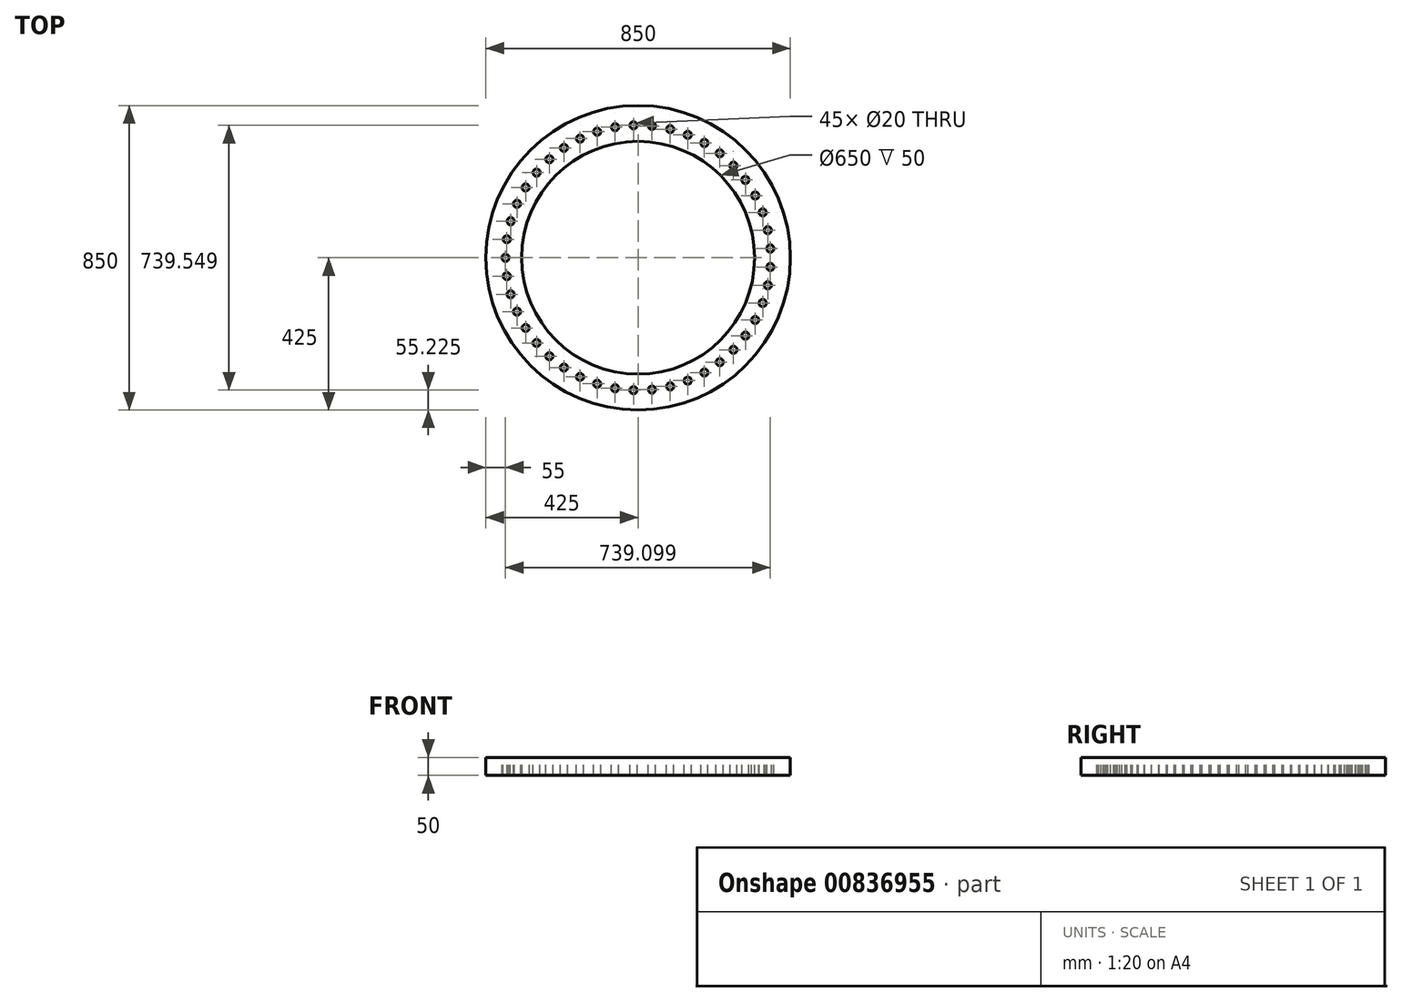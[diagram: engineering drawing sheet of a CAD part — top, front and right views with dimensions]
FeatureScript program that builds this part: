
annotation { "Feature Type Name" : "Feature", "Feature Type Description" : "" }
export const myFeature = defineFeature(function(context is Context, id is Id, definition is map)
    precondition{}
    {
        {
            var Q0;
            Q0=qCreatedBy(makeId("Top.planeOp"),FACE);
            var sketch = newSketch(context, id + "F0", { "sketchPlane" : qUnion([Q0])});
            skLineSegment(sketch, "E0.bottom", {"start": v(-1185, 450) * mm, "end": v(1185, 450) * mm});
            skLineSegment(sketch, "E0.top", {"start": v(-1185, -450) * mm, "end": v(1185, -450) * mm});
            skLineSegment(sketch, "E0.left", {"start": v(-1185, 450) * mm, "end": v(-1185, -450) * mm});
            skLineSegment(sketch, "E0.right", {"start": v(1185, 450) * mm, "end": v(1185, -450) * mm});
            skPoint(sketch, "E0.middle", {"position": v(0, 0) * mm});
            skLineSegment(sketch, "E1.bottom", {"start": v(-1185, 450) * mm, "end": v(-1141.5, 450) * mm});
            skLineSegment(sketch, "E1.top", {"start": v(-1185, -450) * mm, "end": v(-1141.5, -450) * mm});
            skLineSegment(sketch, "E1.right", {"start": v(-1141.49, 450) * mm, "end": v(-1141.49, -450) * mm});
            skLineSegment(sketch, "E2", {"start": v(1185, 0) * mm, "end": v(-1185, 0) * mm, "construction": true});
            skLineSegment(sketch, "E3", {"start": v(-92.5, -600) * mm, "end": v(-92.5, 600) * mm, "construction": true});
            skCircle(sketch, "E4", {"center": v(-92.5, 0) * mm, "radius": 600 * mm});
            skCircle(sketch, "E5", {"center": v(-92.5, 0) * mm, "radius": 550 * mm});
            skCircle(sketch, "E6", {"center": v(-92.5, 0) * mm, "radius": 425 * mm});
            skCircle(sketch, "E7", {"center": v(-92.5, 0) * mm, "radius": 525 * mm});
            skCircle(sketch, "E8", {"center": v(-617.5, 0) * mm, "radius": 10 * mm});
            skCircle(sketch, "E9.1.0", {"center": v(-612.4, -73.07) * mm, "radius": 10 * mm});
            skCircle(sketch, "E9.2.0", {"center": v(-597.16, -144.7) * mm, "radius": 10 * mm});
            skCircle(sketch, "E10.1.3.0", {"center": v(-572.11, -213.54) * mm, "radius": 10 * mm});
            skCircle(sketch, "E10.1.4.0", {"center": v(-537.73, -278.2) * mm, "radius": 10 * mm});
            skCircle(sketch, "E10.1.5.0", {"center": v(-494.67, -337.46) * mm, "radius": 10 * mm});
            skCircle(sketch, "E10.1.6.0", {"center": v(-443.8, -390.15) * mm, "radius": 10 * mm});
            skCircle(sketch, "E10.1.7.0", {"center": v(-386.08, -435.24) * mm, "radius": 10 * mm});
            skCircle(sketch, "E10.1.8.0", {"center": v(-322.64, -471.87) * mm, "radius": 10 * mm});
            skCircle(sketch, "E10.1.9.0", {"center": v(-254.73, -499.3) * mm, "radius": 10 * mm});
            skCircle(sketch, "E10.1.10.0", {"center": v(-183.67, -517.02) * mm, "radius": 10 * mm});
            skCircle(sketch, "E10.1.11.0", {"center": v(-110.82, -524.68) * mm, "radius": 10 * mm});
            skCircle(sketch, "E10.1.12.0", {"center": v(-37.62, -522.12) * mm, "radius": 10 * mm});
            skCircle(sketch, "E10.1.13.0", {"center": v(34.5, -509.4) * mm, "radius": 10 * mm});
            skCircle(sketch, "E10.1.14.0", {"center": v(104.17, -486.77) * mm, "radius": 10 * mm});
            skCircle(sketch, "E10.1.15.0", {"center": v(170, -454.66) * mm, "radius": 10 * mm});
            skCircle(sketch, "E10.1.16.0", {"center": v(230.72, -413.7) * mm, "radius": 10 * mm});
            skCircle(sketch, "E10.1.17.0", {"center": v(285.15, -364.7) * mm, "radius": 10 * mm});
            skCircle(sketch, "E10.1.18.0", {"center": v(332.23, -308.59) * mm, "radius": 10 * mm});
            skCircle(sketch, "E10.1.19.0", {"center": v(371.05, -246.47) * mm, "radius": 10 * mm});
            skCircle(sketch, "E10.1.20.0", {"center": v(400.84, -179.56) * mm, "radius": 10 * mm});
            skCircle(sketch, "E10.1.21.0", {"center": v(421.03, -109.15) * mm, "radius": 10 * mm});
            skCircle(sketch, "E10.1.22.0", {"center": v(431.22, -36.62) * mm, "radius": 10 * mm});
            skCircle(sketch, "E10.1.23.0", {"center": v(431.22, 36.62) * mm, "radius": 10 * mm});
            skCircle(sketch, "E10.1.24.0", {"center": v(421.03, 109.15) * mm, "radius": 10 * mm});
            skCircle(sketch, "E10.1.25.0", {"center": v(400.84, 179.56) * mm, "radius": 10 * mm});
            skCircle(sketch, "E10.1.26.0", {"center": v(371.05, 246.47) * mm, "radius": 10 * mm});
            skCircle(sketch, "E10.1.27.0", {"center": v(332.23, 308.59) * mm, "radius": 10 * mm});
            skCircle(sketch, "E10.1.28.0", {"center": v(285.15, 364.7) * mm, "radius": 10 * mm});
            skCircle(sketch, "E10.1.29.0", {"center": v(230.72, 413.7) * mm, "radius": 10 * mm});
            skCircle(sketch, "E10.1.30.0", {"center": v(170, 454.66) * mm, "radius": 10 * mm});
            skCircle(sketch, "E10.1.31.0", {"center": v(104.17, 486.77) * mm, "radius": 10 * mm});
            skCircle(sketch, "E10.1.32.0", {"center": v(34.5, 509.4) * mm, "radius": 10 * mm});
            skCircle(sketch, "E10.1.33.0", {"center": v(-37.62, 522.12) * mm, "radius": 10 * mm});
            skCircle(sketch, "E10.1.34.0", {"center": v(-110.82, 524.68) * mm, "radius": 10 * mm});
            skCircle(sketch, "E10.1.35.0", {"center": v(-183.67, 517.02) * mm, "radius": 10 * mm});
            skCircle(sketch, "E10.1.36.0", {"center": v(-254.73, 499.3) * mm, "radius": 10 * mm});
            skCircle(sketch, "E10.1.37.0", {"center": v(-322.64, 471.87) * mm, "radius": 10 * mm});
            skCircle(sketch, "E10.1.38.0", {"center": v(-386.08, 435.24) * mm, "radius": 10 * mm});
            skCircle(sketch, "E10.1.39.0", {"center": v(-443.8, 390.15) * mm, "radius": 10 * mm});
            skCircle(sketch, "E10.1.40.0", {"center": v(-494.67, 337.46) * mm, "radius": 10 * mm});
            skCircle(sketch, "E10.1.41.0", {"center": v(-537.73, 278.2) * mm, "radius": 10 * mm});
            skCircle(sketch, "E10.1.42.0", {"center": v(-572.11, 213.54) * mm, "radius": 10 * mm});
            skCircle(sketch, "E10.1.43.0", {"center": v(-597.16, 144.7) * mm, "radius": 10 * mm});
            skCircle(sketch, "E10.1.44.0", {"center": v(-612.4, 73.07) * mm, "radius": 10 * mm});
            skCircle(sketch, "E11", {"center": v(-92.5, 0) * mm, "radius": 370 * mm});
            skCircle(sketch, "E12", {"center": v(-462.5, 0) * mm, "radius": 10 * mm});
            skCircle(sketch, "E13.1.0", {"center": v(-458.9, -51.5) * mm, "radius": 10 * mm});
            skCircle(sketch, "E13.2.0", {"center": v(-448.17, -101.99) * mm, "radius": 10 * mm});
            skCircle(sketch, "E13.3.0", {"center": v(-430.51, -150.5) * mm, "radius": 10 * mm});
            skCircle(sketch, "E13.4.0", {"center": v(-406.28, -196.07) * mm, "radius": 10 * mm});
            skCircle(sketch, "E13.5.0", {"center": v(-375.94, -237.83) * mm, "radius": 10 * mm});
            skCircle(sketch, "E13.6.0", {"center": v(-340.08, -274.96) * mm, "radius": 10 * mm});
            skCircle(sketch, "E13.7.0", {"center": v(-299.4, -306.74) * mm, "radius": 10 * mm});
            skCircle(sketch, "E13.8.0", {"center": v(-254.7, -332.55) * mm, "radius": 10 * mm});
            skCircle(sketch, "E13.9.0", {"center": v(-206.84, -351.9) * mm, "radius": 10 * mm});
            skCircle(sketch, "E13.10.0", {"center": v(-156.75, -364.38) * mm, "radius": 10 * mm});
            skCircle(sketch, "E13.11.0", {"center": v(-105.41, -369.77) * mm, "radius": 10 * mm});
            skCircle(sketch, "E13.12.0", {"center": v(-53.82, -367.97) * mm, "radius": 10 * mm});
            skCircle(sketch, "E13.13.0", {"center": v(-2.99, -359) * mm, "radius": 10 * mm});
            skCircle(sketch, "E13.14.0", {"center": v(46.1, -343.06) * mm, "radius": 10 * mm});
            skCircle(sketch, "E13.15.0", {"center": v(92.5, -320.43) * mm, "radius": 10 * mm});
            skCircle(sketch, "E13.16.0", {"center": v(135.3, -291.56) * mm, "radius": 10 * mm});
            skCircle(sketch, "E13.17.0", {"center": v(173.66, -257.02) * mm, "radius": 10 * mm});
            skCircle(sketch, "E13.18.0", {"center": v(206.84, -217.48) * mm, "radius": 10 * mm});
            skCircle(sketch, "E13.19.0", {"center": v(234.2, -173.7) * mm, "radius": 10 * mm});
            skCircle(sketch, "E13.20.0", {"center": v(255.19, -126.55) * mm, "radius": 10 * mm});
            skCircle(sketch, "E13.21.0", {"center": v(269.41, -76.93) * mm, "radius": 10 * mm});
            skCircle(sketch, "E13.22.0", {"center": v(276.6, -25.8) * mm, "radius": 10 * mm});
            skCircle(sketch, "E13.23.0", {"center": v(276.6, 25.8) * mm, "radius": 10 * mm});
            skCircle(sketch, "E13.24.0", {"center": v(269.41, 76.93) * mm, "radius": 10 * mm});
            skCircle(sketch, "E13.25.0", {"center": v(255.19, 126.55) * mm, "radius": 10 * mm});
            skCircle(sketch, "E13.26.0", {"center": v(234.2, 173.7) * mm, "radius": 10 * mm});
            skCircle(sketch, "E13.27.0", {"center": v(206.84, 217.48) * mm, "radius": 10 * mm});
            skCircle(sketch, "E13.28.0", {"center": v(173.66, 257.02) * mm, "radius": 10 * mm});
            skCircle(sketch, "E13.29.0", {"center": v(135.3, 291.56) * mm, "radius": 10 * mm});
            skCircle(sketch, "E13.30.0", {"center": v(92.5, 320.43) * mm, "radius": 10 * mm});
            skCircle(sketch, "E13.31.0", {"center": v(46.1, 343.06) * mm, "radius": 10 * mm});
            skCircle(sketch, "E13.32.0", {"center": v(-2.99, 359) * mm, "radius": 10 * mm});
            skCircle(sketch, "E13.33.0", {"center": v(-53.82, 367.97) * mm, "radius": 10 * mm});
            skCircle(sketch, "E13.34.0", {"center": v(-105.41, 369.77) * mm, "radius": 10 * mm});
            skCircle(sketch, "E13.35.0", {"center": v(-156.75, 364.38) * mm, "radius": 10 * mm});
            skCircle(sketch, "E13.36.0", {"center": v(-206.84, 351.9) * mm, "radius": 10 * mm});
            skCircle(sketch, "E13.37.0", {"center": v(-254.7, 332.55) * mm, "radius": 10 * mm});
            skCircle(sketch, "E13.38.0", {"center": v(-299.4, 306.74) * mm, "radius": 10 * mm});
            skCircle(sketch, "E13.39.0", {"center": v(-340.08, 274.96) * mm, "radius": 10 * mm});
            skCircle(sketch, "E13.40.0", {"center": v(-375.94, 237.83) * mm, "radius": 10 * mm});
            skCircle(sketch, "E13.41.0", {"center": v(-406.28, 196.07) * mm, "radius": 10 * mm});
            skCircle(sketch, "E13.42.0", {"center": v(-430.51, 150.5) * mm, "radius": 10 * mm});
            skCircle(sketch, "E13.43.0", {"center": v(-448.17, 101.99) * mm, "radius": 10 * mm});
            skCircle(sketch, "E13.44.0", {"center": v(-458.9, 51.5) * mm, "radius": 10 * mm});
            skLineSegment(sketch, "E14.bottom", {"start": v(-925, 450) * mm, "end": v(-735, 450) * mm});
            skLineSegment(sketch, "E14.top", {"start": v(-925, 315) * mm, "end": v(-735, 315) * mm});
            skLineSegment(sketch, "E14.left", {"start": v(-925, 450) * mm, "end": v(-925, 315) * mm});
            skLineSegment(sketch, "E14.right", {"start": v(-735, 450) * mm, "end": v(-735, 315) * mm});
            skLineSegment(sketch, "E15.bottom", {"start": v(-913, 327) * mm, "end": v(-747, 327) * mm});
            skLineSegment(sketch, "E15.top", {"start": v(-913, 438) * mm, "end": v(-747, 438) * mm});
            skLineSegment(sketch, "E15.left", {"start": v(-913, 327) * mm, "end": v(-913, 438) * mm});
            skLineSegment(sketch, "E15.right", {"start": v(-747, 327) * mm, "end": v(-747, 438) * mm});
            skPoint(sketch, "E15.middle", {"position": v(-830, 382.5) * mm});
            skLineSegment(sketch, "E16.MirrorCS", {"start": v(-735, -450) * mm, "end": v(-735, -315) * mm});
            skLineSegment(sketch, "E17.MirrorCS", {"start": v(-925, -315) * mm, "end": v(-735, -315) * mm});
            skLineSegment(sketch, "E18.MirrorCS", {"start": v(-913, -438) * mm, "end": v(-747, -438) * mm});
            skLineSegment(sketch, "E19.MirrorCS", {"start": v(-925, -450) * mm, "end": v(-925, -315) * mm});
            skLineSegment(sketch, "E20.MirrorCS", {"start": v(-747, -327) * mm, "end": v(-747, -438) * mm});
            skPoint(sketch, "E21.MirrorP", {"position": v(-830, -382.5) * mm});
            skLineSegment(sketch, "E22.MirrorCS", {"start": v(-913, -327) * mm, "end": v(-913, -438) * mm});
            skLineSegment(sketch, "E23.MirrorCS", {"start": v(-913, -327) * mm, "end": v(-747, -327) * mm});
            skLineSegment(sketch, "E24.MirrorCS", {"start": v(-925, -450) * mm, "end": v(-735, -450) * mm});
            skArc(sketch, "E25", {"start": v(-301.83, -562.3) * mm, "mid": v(-739.86, -478.19) * mm, "end": v(-1185, -450) * mm});
            skArc(sketch, "E26.MirrorCS", {"start": v(-301.83, 562.3) * mm, "mid": v(-739.86, 478.19) * mm, "end": v(-1185, 450) * mm});
            skCircle(sketch, "E27", {"center": v(-92.5, 0) * mm, "radius": 325 * mm});
            skSolve(sketch);
        }
        {
            var Q0;
            {var subQ130=sQuery(id+"F0.wireOp",EDGE,"E6");var subQ131=makeQuery(id+"F0.imprint","INTERSECT",VERTEX,{"derivedFrom":[sQuery(id+"F0.wireOp",EDGE,"E0.bottom"),subQ130]});Q0=makeQuery(id+"F0.imprint","IMPRINT",FACE,{"disambiguationData":[TD([[makeQuery(id+"F0.imprint","IMPRINT",EDGE,{"disambiguationData":[TD([[subQ131,-1.0]])],"derivedFrom":subQ130}),1.0]])]});}
            var Q1;
            Q1=makeQuery(id+"F0.imprint","IMPRINT",FACE,{"disambiguationData":[TD([[makeQuery(id+"F0.imprint","IMPRINT",EDGE,{"derivedFrom":sQuery(id+"F0.wireOp",EDGE,"E27")}),-1.0]])]});
            extrude(context, id + "F1", {"entities" : qUnion([Q0, Q1]), "oppositeDirection" : true, "depth" : 50 * mm, "offsetDistance" : 25 * mm});
        }
    });
